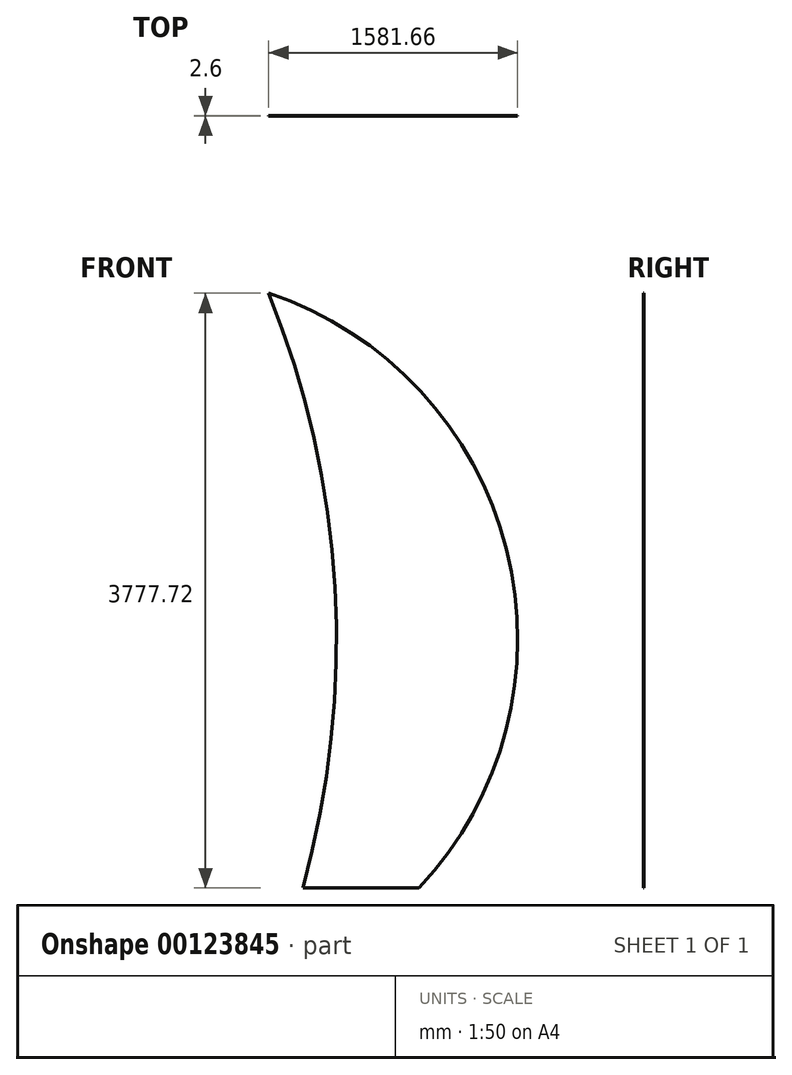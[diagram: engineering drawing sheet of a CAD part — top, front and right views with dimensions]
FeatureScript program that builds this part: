
annotation { "Feature Type Name" : "Feature", "Feature Type Description" : "" }
export const myFeature = defineFeature(function(context is Context, id is Id, definition is map)
    precondition{}
    {
        {
            var Q0;
            Q0=qCreatedBy(makeId("Front.planeOp"),FACE);
            var sketch = newSketch(context, id + "F0", { "sketchPlane" : qUnion([Q0])});
            skArc(sketch, "E0", {"start": v(-595.13, -1875.45) * mm, "mid": v(-390.9, 31.35) * mm, "end": v(-811.98, 1902.27) * mm});
            skArc(sketch, "E1", {"start": v(144.49, -1875.45) * mm, "mid": v(698.87, 274.85) * mm, "end": v(-811.98, 1902.27) * mm});
            skPoint(sketch, "E2.startSnap0", {"position": v(694.2, -287.6) * mm});
            skLineSegment(sketch, "E3", {"start": v(-595.13, -1875.45) * mm, "end": v(-516.84, -1875.45) * mm});
            skPoint(sketch, "E4.orphan", {"position": v(556.97, -1148.42) * mm});
            skLineSegment(sketch, "E5.trimOffspring", {"start": v(39.5, -1875.45) * mm, "end": v(144.49, -1875.45) * mm});
            skPoint(sketch, "E6.orphan", {"position": v(767.4, -190.62) * mm});
            skPoint(sketch, "E7.orphan", {"position": v(767.4, -287.6) * mm});
            skLineSegment(sketch, "E8", {"start": v(-516.84, -1875.45) * mm, "end": v(39.5, -1875.45) * mm});
            skSolve(sketch);
        }
        {
            var Q0;
            Q0=makeQuery(id+"F0.imprint","IMPRINT",FACE,{"disambiguationData":[TD([[makeQuery(id+"F0.imprint","IMPRINT",EDGE,{"derivedFrom":sQuery(id+"F0.wireOp",EDGE,"E0")}),-1.0]])]});
            extrude(context, id + "F1", {"entities" : qUnion([Q0]), "oppositeDirection" : true, "depth" : 2.6 * mm});
        }
    });
